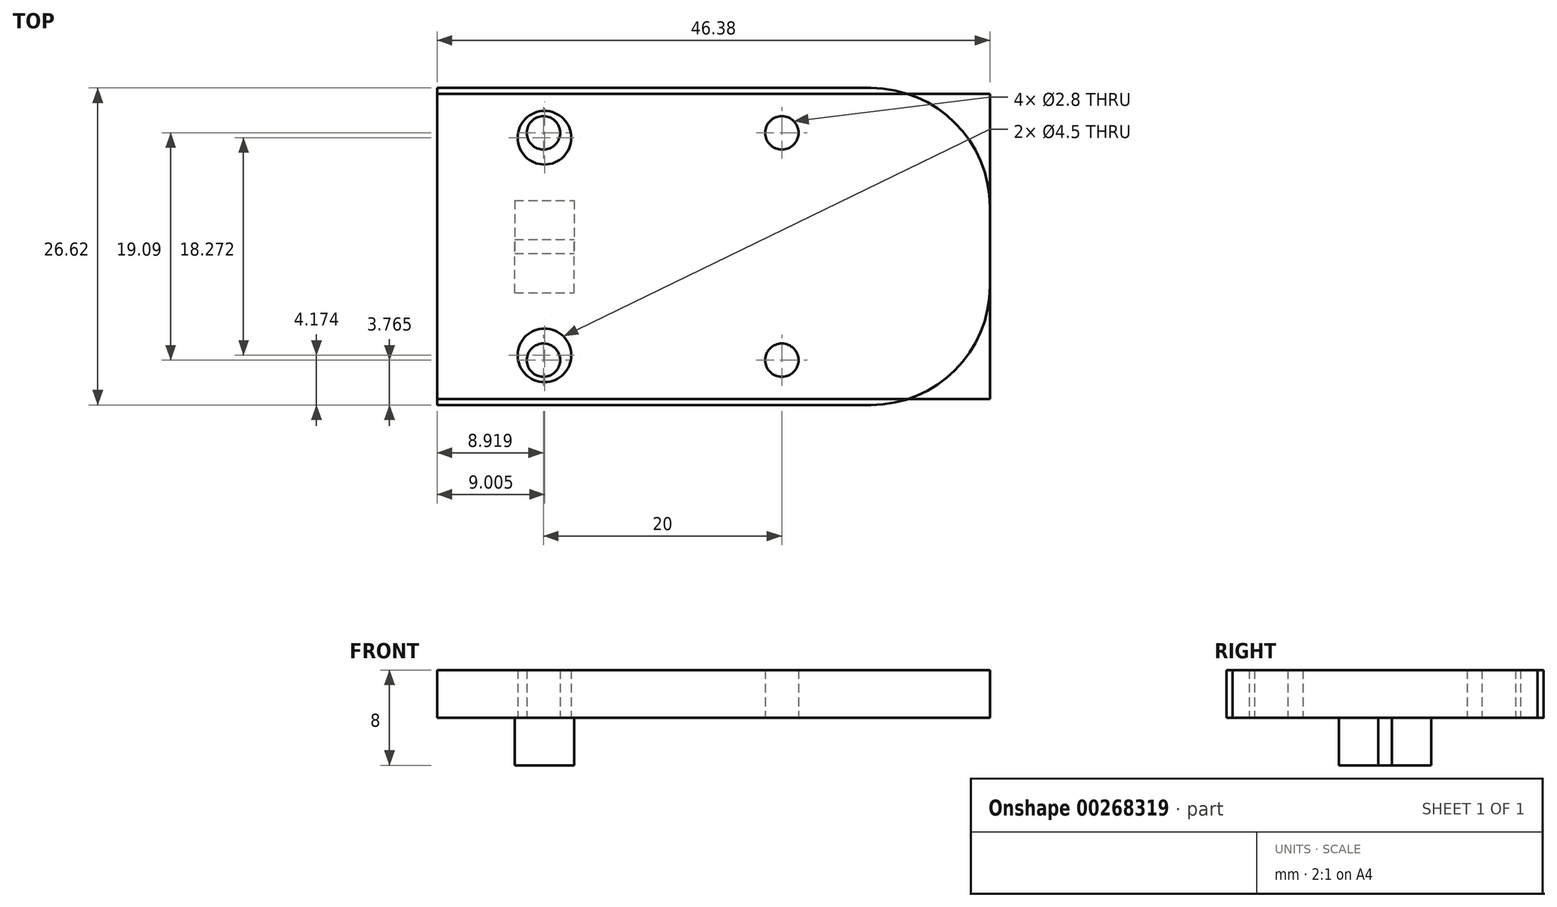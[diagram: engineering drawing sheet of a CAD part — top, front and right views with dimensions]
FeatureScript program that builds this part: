
annotation { "Feature Type Name" : "Feature", "Feature Type Description" : "" }
export const myFeature = defineFeature(function(context is Context, id is Id, definition is map)
    precondition{}
    {
        {
            var Q0;
            Q0=qCreatedBy(makeId("Top.planeOp"),FACE);
            var sketch = newSketch(context, id + "F0", { "sketchPlane" : qUnion([Q0])});
            skLineSegment(sketch, "E0.bottom", {"start": v(-43.89, 13.31) * mm, "end": v(2.5, 13.31) * mm});
            skLineSegment(sketch, "E0.top", {"start": v(-43.89, -12.8) * mm, "end": v(2.5, -12.8) * mm});
            skLineSegment(sketch, "E0.left", {"start": v(-43.89, 13.31) * mm, "end": v(-43.89, -12.8) * mm});
            skLineSegment(sketch, "E0.right", {"start": v(2.5, 13.31) * mm, "end": v(2.5, -12.8) * mm});
            skCircle(sketch, "E1", {"center": v(-34.89, 9.14) * mm, "radius": 2.25 * mm});
            skCircle(sketch, "E2", {"center": v(-34.97, -9.54) * mm, "radius": 1.4 * mm});
            skCircle(sketch, "E3", {"center": v(-14.97, -9.54) * mm, "radius": 1.4 * mm});
            skSolve(sketch);
        }
        {
            var Q0;
            Q0=qSketchRegion(id+"F0",true);
            extrude(context, id + "F1", {"entities" : qUnion([Q0]), "depth" : 4 * mm});
        }
        {
            var Q0;
            Q0=makeQuery(id+"F1.opExtrude","CAP_FACE",FACE,{"disambiguationData":[OSD([sQuery(id+"F0.wireOp",EDGE,"E0.bottom"),sQuery(id+"F0.wireOp",EDGE,"E0.top"),sQuery(id+"F0.wireOp",EDGE,"E0.left"),sQuery(id+"F0.wireOp",EDGE,"E0.right"),sQuery(id+"F0.wireOp",EDGE,"E1"),sQuery(id+"F0.wireOp",EDGE,"E2"),sQuery(id+"F0.wireOp",EDGE,"E3")])],"isStart":true});
            var sketch = newSketch(context, id + "F2", { "sketchPlane" : qUnion([Q0])});
            skLineSegment(sketch, "E4.bottom", {"start": v(-37.39, 3.87) * mm, "end": v(-32.39, 3.87) * mm});
            skLineSegment(sketch, "E4.top", {"start": v(-37.39, -0.58) * mm, "end": v(-32.39, -0.58) * mm});
            skLineSegment(sketch, "E4.left", {"start": v(-37.39, 3.87) * mm, "end": v(-37.39, -0.58) * mm});
            skLineSegment(sketch, "E4.right", {"start": v(-32.39, 3.87) * mm, "end": v(-32.39, -0.58) * mm});
            skLineSegment(sketch, "E5", {"start": v(-34.89, -9.14) * mm, "end": v(-34.89, 5.1) * mm, "construction": true});
            skSolve(sketch);
        }
        {
            var Q0;
            Q0=qSketchRegion(id+"F2",true);
            extrude(context, id + "F3", {"entities" : qUnion([Q0]), "operationType" : NewBodyOperationType.ADD, "depth" : 4 * mm});
        }
        {
            var Q0;
            Q0=makeQuery(id+"F1.opExtrude","SWEPT_EDGE",EDGE,{"disambiguationData":[OSD([sQuery(id+"F0.wireOp",EDGE,"E0.bottom"),sQuery(id+"F0.wireOp",EDGE,"E0.right")])]});
            fillet(context, id + "F4", {"entities" : qUnion([Q0]), "radius" : 10 * mm, "tangentPropagation" : true, "allowEdgeOverflow" : false});
        }
        {
            var Q0;
            Q0=makeQuery(id+"F1.opExtrude","SWEPT_BODY",BODY,{"disambiguationData":[OSD([sQuery(id+"F0.wireOp",EDGE,"E0.bottom"),sQuery(id+"F0.wireOp",EDGE,"E0.top"),sQuery(id+"F0.wireOp",EDGE,"E0.left"),sQuery(id+"F0.wireOp",EDGE,"E0.right"),sQuery(id+"F0.wireOp",EDGE,"E1"),sQuery(id+"F0.wireOp",EDGE,"E2"),sQuery(id+"F0.wireOp",EDGE,"E3")])]});
            var Q1;
            Q1=qCreatedBy(makeId("Front.planeOp"),FACE);
            mirror(context, id + "F5", {"entities" : qUnion([Q0]), "mirrorPlane" : qUnion([Q1])});
        }
    });
